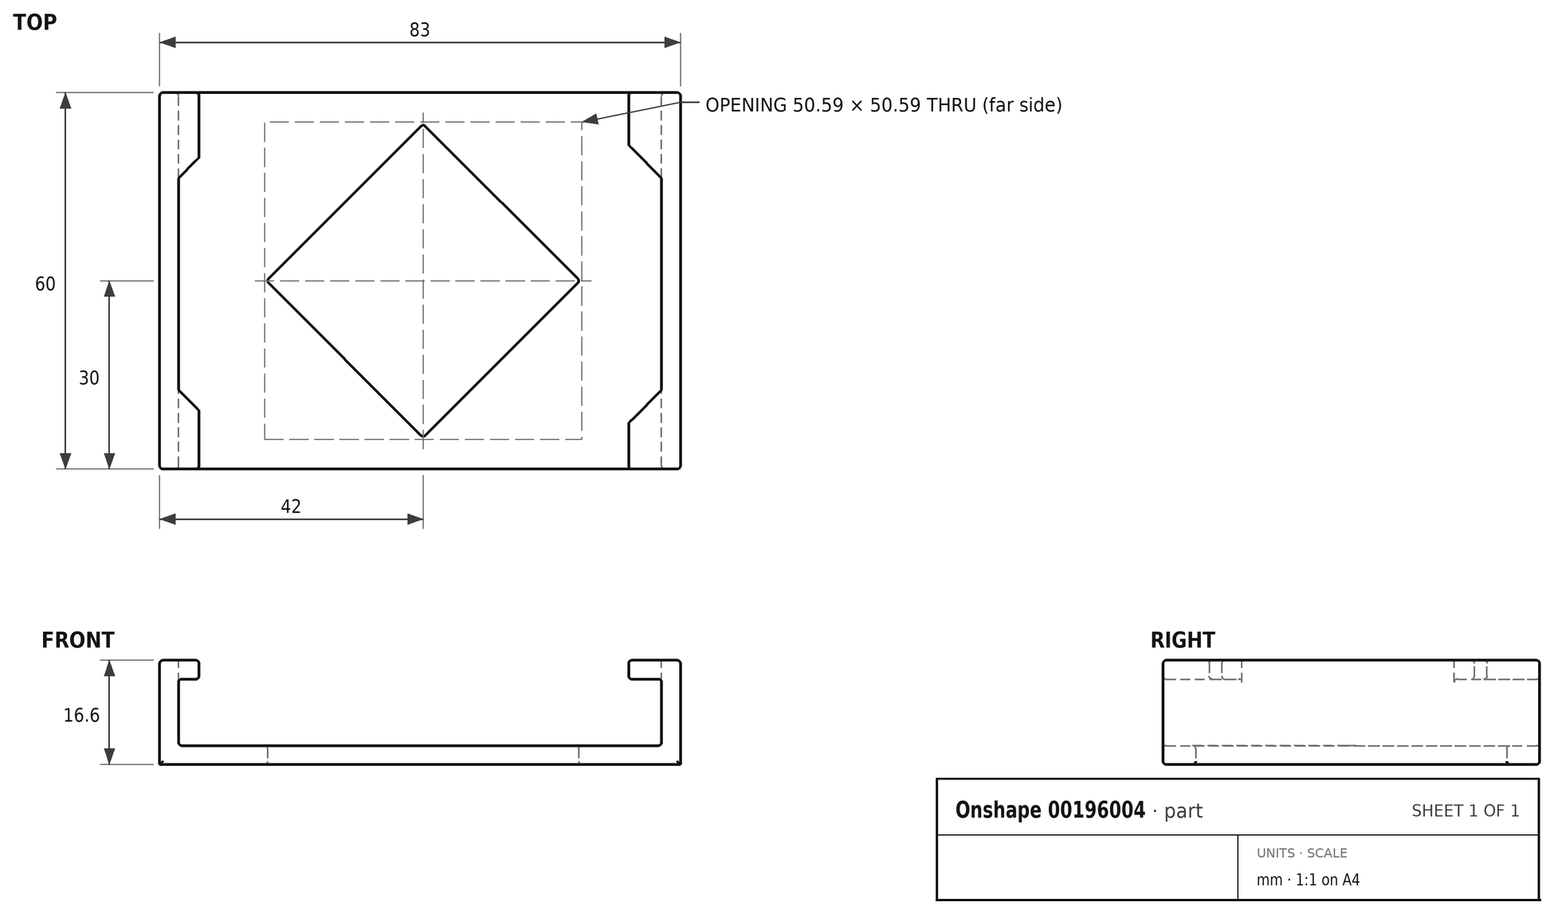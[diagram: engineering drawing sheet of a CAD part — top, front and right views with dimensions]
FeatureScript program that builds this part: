
annotation { "Feature Type Name" : "Feature", "Feature Type Description" : "" }
export const myFeature = defineFeature(function(context is Context, id is Id, definition is map)
    precondition{}
    {
        {
            var Q0;
            Q0=qCreatedBy(makeId("Front.planeOp"),FACE);
            var sketch = newSketch(context, id + "F0", { "sketchPlane" : qUnion([Q0])});
            skLineSegment(sketch, "E0", {"start": v(-51.95, -23.65) * mm, "end": v(-13.62, -23.65) * mm});
            skLineSegment(sketch, "E1", {"start": v(-13.62, -20.65) * mm, "end": v(-48.95, -20.65) * mm});
            skLineSegment(sketch, "E2", {"start": v(-48.95, -20.65) * mm, "end": v(-48.95, -10.05) * mm});
            skLineSegment(sketch, "E3", {"start": v(-48.95, -10.05) * mm, "end": v(-45.7, -10.05) * mm});
            skLineSegment(sketch, "E4", {"start": v(-45.7, -10.05) * mm, "end": v(-45.7, -7.05) * mm});
            skLineSegment(sketch, "E5", {"start": v(-45.7, -7.05) * mm, "end": v(-51.95, -7.05) * mm});
            skLineSegment(sketch, "E6", {"start": v(-51.95, -7.05) * mm, "end": v(-51.95, -23.65) * mm});
            skLineSegment(sketch, "E7.MirrorCS", {"start": v(31.05, -7.05) * mm, "end": v(31.05, -23.65) * mm});
            skLineSegment(sketch, "E8.MirrorCS", {"start": v(22.8, -7.05) * mm, "end": v(31.05, -7.05) * mm});
            skLineSegment(sketch, "E9.MirrorCS", {"start": v(22.8, -10.05) * mm, "end": v(22.8, -7.05) * mm});
            skLineSegment(sketch, "E10.MirrorCS", {"start": v(28.05, -10.05) * mm, "end": v(22.8, -10.05) * mm});
            skLineSegment(sketch, "E11.MirrorCS", {"start": v(28.05, -20.65) * mm, "end": v(28.05, -10.05) * mm});
            skLineSegment(sketch, "E12.MirrorCS", {"start": v(31.05, -23.65) * mm, "end": v(-7.68, -23.65) * mm});
            skLineSegment(sketch, "E13.MirrorCS", {"start": v(-7.68, -20.65) * mm, "end": v(28.05, -20.65) * mm});
            skLineSegment(sketch, "E14", {"start": v(-13.62, -20.65) * mm, "end": v(-7.68, -20.65) * mm});
            skLineSegment(sketch, "E15", {"start": v(-13.62, -23.65) * mm, "end": v(-7.68, -23.65) * mm});
            skSolve(sketch);
        }
        {
            var Q0;
            Q0 = qSketchRegion(id + "F0", true);
            extrude(context, id + "F1", {"entities" : qUnion([Q0]), "depth" : 60 * mm});
        }
        {
            var Q0;
            Q0=makeQuery(id+"F1.opExtrude","SWEPT_FACE",FACE,{"disambiguationData":[OSD([sQuery(id+"F0.wireOp",EDGE,"E3")])]});
            fillet(context, id + "F2", {"entities" : qUnion([Q0]), "radius" : 0.5 * mm, "tangentPropagation" : true, "allowEdgeOverflow" : false});
        }
        {
            var Q0;
            Q0=makeQuery(id+"F1.opExtrude","SWEPT_FACE",FACE,{"disambiguationData":[OSD([sQuery(id+"F0.wireOp",EDGE,"E10.MirrorCS")])]});
            fillet(context, id + "F3", {"entities" : qUnion([Q0]), "radius" : 0.5 * mm, "tangentPropagation" : true, "allowEdgeOverflow" : false});
        }
        {
            var Q0;
            Q0=makeQuery(id+"F1.opExtrude","SWEPT_FACE",FACE,{"disambiguationData":[OSD([sQuery(id+"F0.wireOp",EDGE,"E1"),sQuery(id+"F0.wireOp",EDGE,"E13.MirrorCS"),sQuery(id+"F0.wireOp",EDGE,"E14")])]});
            fillet(context, id + "F4", {"entities" : qUnion([Q0]), "radius" : 0.5 * mm, "tangentPropagation" : true, "allowEdgeOverflow" : false});
        }
        {
            var Q0;
            Q0=makeQuery(id+"F1.opExtrude","SWEPT_FACE",FACE,{"disambiguationData":[OSD([sQuery(id+"F0.wireOp",EDGE,"E5")])]});
            var Q1;
            Q1=makeQuery(id+"F1.opExtrude","SWEPT_FACE",FACE,{"disambiguationData":[OSD([sQuery(id+"F0.wireOp",EDGE,"E8.MirrorCS")])]});
            var Q2;
            Q2=makeQuery(id+"F1.opExtrude","SWEPT_FACE",FACE,{"disambiguationData":[OSD([sQuery(id+"F0.wireOp",EDGE,"E9.MirrorCS")])]});
            var Q3;
            Q3=makeQuery(id+"F1.opExtrude","SWEPT_FACE",FACE,{"disambiguationData":[OSD([sQuery(id+"F0.wireOp",EDGE,"E4")])]});
            var Q4;
            Q4=makeQuery(id+"F1.opExtrude","CAP_FACE",FACE,{"disambiguationData":[OSD([sQuery(id+"F0.wireOp",EDGE,"E0"),sQuery(id+"F0.wireOp",EDGE,"E1"),sQuery(id+"F0.wireOp",EDGE,"E2"),sQuery(id+"F0.wireOp",EDGE,"E3"),sQuery(id+"F0.wireOp",EDGE,"E4"),sQuery(id+"F0.wireOp",EDGE,"E5"),sQuery(id+"F0.wireOp",EDGE,"E6"),sQuery(id+"F0.wireOp",EDGE,"E7.MirrorCS"),sQuery(id+"F0.wireOp",EDGE,"E8.MirrorCS"),sQuery(id+"F0.wireOp",EDGE,"E9.MirrorCS"),sQuery(id+"F0.wireOp",EDGE,"E10.MirrorCS"),sQuery(id+"F0.wireOp",EDGE,"E11.MirrorCS"),sQuery(id+"F0.wireOp",EDGE,"E12.MirrorCS"),sQuery(id+"F0.wireOp",EDGE,"E13.MirrorCS"),sQuery(id+"F0.wireOp",EDGE,"E14"),sQuery(id+"F0.wireOp",EDGE,"E15")])],"isStart":false});
            var Q5;
            Q5=makeQuery(id+"F1.opExtrude","CAP_FACE",FACE,{"disambiguationData":[OSD([sQuery(id+"F0.wireOp",EDGE,"E0"),sQuery(id+"F0.wireOp",EDGE,"E1"),sQuery(id+"F0.wireOp",EDGE,"E2"),sQuery(id+"F0.wireOp",EDGE,"E3"),sQuery(id+"F0.wireOp",EDGE,"E4"),sQuery(id+"F0.wireOp",EDGE,"E5"),sQuery(id+"F0.wireOp",EDGE,"E6"),sQuery(id+"F0.wireOp",EDGE,"E7.MirrorCS"),sQuery(id+"F0.wireOp",EDGE,"E8.MirrorCS"),sQuery(id+"F0.wireOp",EDGE,"E9.MirrorCS"),sQuery(id+"F0.wireOp",EDGE,"E10.MirrorCS"),sQuery(id+"F0.wireOp",EDGE,"E11.MirrorCS"),sQuery(id+"F0.wireOp",EDGE,"E12.MirrorCS"),sQuery(id+"F0.wireOp",EDGE,"E13.MirrorCS"),sQuery(id+"F0.wireOp",EDGE,"E14"),sQuery(id+"F0.wireOp",EDGE,"E15")])],"isStart":true});
            fillet(context, id + "F5", {"entities" : qUnion([Q0, Q1, Q2, Q3, Q4, Q5]), "radius" : 0.5 * mm, "tangentPropagation" : true, "allowEdgeOverflow" : false});
        }
        {
            var Q0;
            Q0=qCreatedBy(makeId("Top.planeOp"),FACE);
            var sketch = newSketch(context, id + "F6", { "sketchPlane" : qUnion([Q0])});
            skLineSegment(sketch, "E16", {"start": v(17.1, -2.67) * mm, "end": v(28.05, -13.62) * mm});
            skLineSegment(sketch, "E17", {"start": v(28.05, -13.62) * mm, "end": v(28.05, -47.4) * mm});
            skLineSegment(sketch, "E18", {"start": v(28.05, -47.4) * mm, "end": v(17.1, -58.35) * mm});
            skLineSegment(sketch, "E19", {"start": v(17.1, -58.35) * mm, "end": v(17.1, -2.67) * mm});
            skLineSegment(sketch, "E20", {"start": v(-48.95, -13.62) * mm, "end": v(-38, -2.67) * mm});
            skLineSegment(sketch, "E21", {"start": v(-38, -2.67) * mm, "end": v(-38, -58.35) * mm});
            skLineSegment(sketch, "E22", {"start": v(-38, -58.35) * mm, "end": v(-48.95, -47.4) * mm});
            skLineSegment(sketch, "E23", {"start": v(-48.95, -47.4) * mm, "end": v(-48.95, -13.62) * mm});
            skSolve(sketch);
        }
        {
            var Q0;
            Q0 = qSketchRegion(id + "F6", true);
            extrude(context, id + "F7", {"entities" : qUnion([Q0]), "operationType" : NewBodyOperationType.REMOVE, "oppositeDirection" : true, "depth" : 12 * mm});
        }
        {
            var Q0;
            Q0=qCreatedBy(makeId("Top.planeOp"),FACE);
            var sketch = newSketch(context, id + "F8", { "sketchPlane" : qUnion([Q0])});
            skCircle(sketch, "E24.cCircle", {"center": v(-9.95, -30) * mm, "radius": 17.68 * mm, "construction": true});
            skLineSegment(sketch, "E24.0", {"start": v(-9.95, -55) * mm, "end": v(-34.95, -30) * mm});
            skLineSegment(sketch, "E24.1", {"start": v(-34.95, -30) * mm, "end": v(-9.95, -5) * mm});
            skLineSegment(sketch, "E24.2", {"start": v(-9.95, -5) * mm, "end": v(15.05, -30) * mm});
            skLineSegment(sketch, "E24.3", {"start": v(15.05, -30) * mm, "end": v(-9.95, -55) * mm});
            skPoint(sketch, "E24.0.midPoint", {"position": v(-22.45, -42.5) * mm});
            skSolve(sketch);
        }
        {
            var Q0;
            Q0 = qSketchRegion(id + "F8", true);
            extrude(context, id + "F9", {"entities" : qUnion([Q0]), "operationType" : NewBodyOperationType.REMOVE, "oppositeDirection" : true, "depth" : 25 * mm});
        }
        {
            var Q0;
            Q0=makeQuery(id+"F9.boolean.opBoolean","COPY",FACE,{"derivedFrom":makeQuery(id+"F9.opExtrude","SWEPT_FACE",FACE,{"disambiguationData":[OSD([sQuery(id+"F8.wireOp",EDGE,"E24.3")])]})});
            var Q1;
            Q1=makeQuery(id+"F9.boolean.opBoolean","COPY",FACE,{"derivedFrom":makeQuery(id+"F9.opExtrude","SWEPT_FACE",FACE,{"disambiguationData":[OSD([sQuery(id+"F8.wireOp",EDGE,"E24.0")])]})});
            var Q2;
            Q2=makeQuery(id+"F9.boolean.opBoolean","COPY",FACE,{"derivedFrom":makeQuery(id+"F9.opExtrude","SWEPT_FACE",FACE,{"disambiguationData":[OSD([sQuery(id+"F8.wireOp",EDGE,"E24.1")])]})});
            var Q3;
            Q3=makeQuery(id+"F9.boolean.opBoolean","COPY",FACE,{"derivedFrom":makeQuery(id+"F9.opExtrude","SWEPT_FACE",FACE,{"disambiguationData":[OSD([sQuery(id+"F8.wireOp",EDGE,"E24.2")])]})});
            fillet(context, id + "F10", {"entities" : qUnion([Q0, Q1, Q2, Q3]), "radius" : 0.5 * mm, "tangentPropagation" : true, "allowEdgeOverflow" : false});
        }
    });
